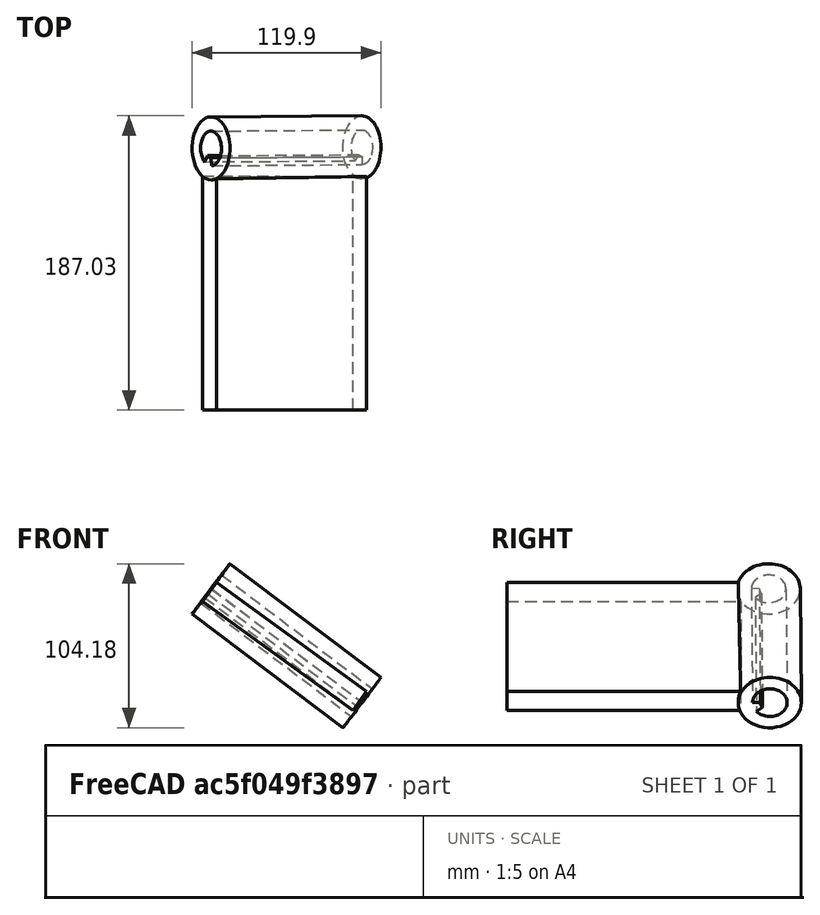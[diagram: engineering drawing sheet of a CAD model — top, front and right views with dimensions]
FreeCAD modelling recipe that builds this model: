
FCSTD DOCUMENT  (FreeCAD 0.16R6704 (Git))
Label: Object 8 right
License: All rights reserved
LicenseURL: http://en.wikipedia.org/wiki/All_rights_reserved
objects: Part::Cylinder×6, Part::Cut×4, Part::MultiFuse×2, Part::Box×1
note: 13 computed .brp shape members not serialized (recipe doc carries the construction recipe); baked Part::Feature solids carry a one-line shape summary decoded from their .brp

FEATURE [Part::Cylinder] Cylinder284  label="Cilindro171"
  Angle = 360
  Height = 120
  Placement = pos=(-292,0,98.9) rot=(0,1,0;2.19911rad)
  Radius = 20
FEATURE [Part::Cylinder] Cylinder285  label="Cilindro172"
  Angle = 360
  Height = 120
  Placement = pos=(-292,0,98.9) rot=(0,1,0;2.19911rad)
  Radius = 11
FEATURE [Part::Cut] Cut301
  Base = -> Cylinder284
  Tool = -> Cylinder285
FEATURE [Part::Cylinder] Cylinder286  label="Cilindro173"
  Angle = 50
  Height = 120
  Placement = pos=(-292,0,98.9) rot=(0,1,0;2.19911rad)
  Radius = 11
FEATURE [Part::Cylinder] Cylinder287  label="Cilindro174"
  Angle = 360
  Height = 130
  Placement = pos=(-292,0,98.9) rot=(0,1,0;2.19911rad)
  Radius = 5
FEATURE [Part::Cut] Cut302
  Base = -> Cylinder286
  Tool = -> Cylinder287
FEATURE [Part::Cylinder] Cylinder288  label="Cilindro175"
  Angle = 90
  Height = 120
  Placement = pos=(-292,0,98.9) rot=(0,1,0;2.19911rad)
  Radius = 11
FEATURE [Part::Cylinder] Cylinder289  label="Cilindro176"
  Angle = 360
  Height = 130
  Placement = pos=(-292,0,98.9) rot=(0,1,0;2.19911rad)
  Radius = 6
FEATURE [Part::Cut] Cut303
  Base = -> Cylinder288
  Tool = -> Cylinder289
FEATURE [Part::Cut] Cut304
  Base = -> Cut303
  Tool = -> Cut302
FEATURE [Part::MultiFuse] Fusion080  label="Fusion089"
  Placement = pos=(-629.788,516.45,-238.137) rot=(0.803158,-0.000129,-0.595767;3.81837rad)
  Shapes = -> [Cut301,Cut304]
FEATURE [Part::Box] Box131  label="Cubo094"
  Height = 15
  Length = 118
  Placement = pos=(-827,291,-12) rot=(0,1,0;0.628319rad)
  Width = 150
FEATURE [Part::MultiFuse] Fusion081  label="(Obj 8 right) Fusion090"
  Placement = pos=(6,0,-3) rot=(0,0,1;0rad)
  Shapes = -> [Fusion080,Box131]
